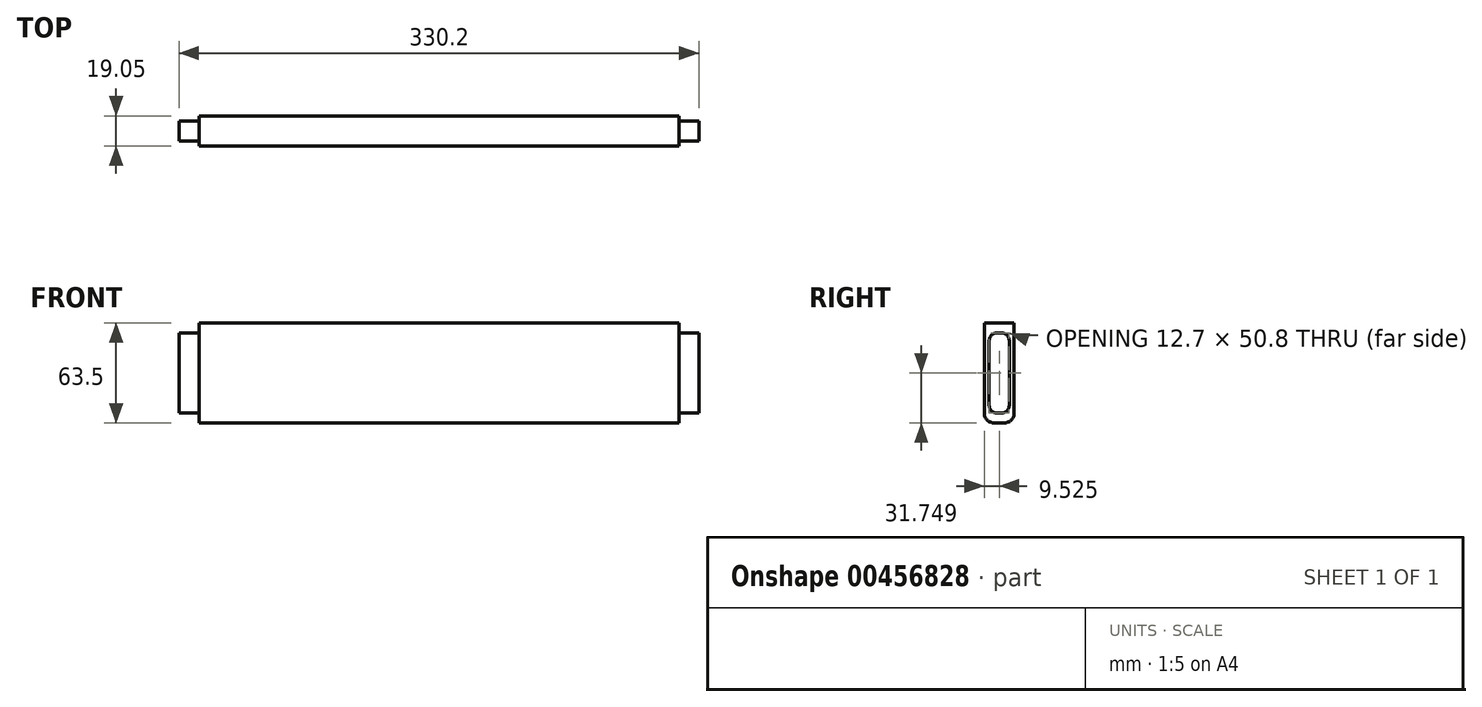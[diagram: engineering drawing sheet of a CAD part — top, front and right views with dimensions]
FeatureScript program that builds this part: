
annotation { "Feature Type Name" : "Feature", "Feature Type Description" : "" }
export const myFeature = defineFeature(function(context is Context, id is Id, definition is map)
    precondition{}
    {
        {
            var Q0;
            Q0=qCreatedBy(makeId("Front.planeOp"),FACE);
            var sketch = newSketch(context, id + "F0", { "sketchPlane" : qUnion([Q0])});
            skLineSegment(sketch, "E0.bottom", {"start": v(-64.17, 31.3) * mm, "end": v(240.63, 31.3) * mm});
            skLineSegment(sketch, "E0.top", {"start": v(-64.17, -32.2) * mm, "end": v(240.63, -32.2) * mm});
            skLineSegment(sketch, "E0.left", {"start": v(-64.17, 31.3) * mm, "end": v(-64.17, -32.2) * mm});
            skLineSegment(sketch, "E0.right", {"start": v(240.63, 31.3) * mm, "end": v(240.63, -32.2) * mm});
            skSolve(sketch);
        }
        {
            var Q0;
            Q0=makeQuery(id+"F0.imprint","IMPRINT",FACE,{"disambiguationData":[TD([[makeQuery(id+"F0.imprint","IMPRINT",EDGE,{"derivedFrom":sQuery(id+"F0.wireOp",EDGE,"E0.bottom")}),-1.0]])]});
            extrude(context, id + "F1", {"entities" : qUnion([Q0]), "oppositeDirection" : true, "depth" : 19.05 * mm});
        }
        {
            var Q0;
            Q0=makeQuery(id+"F1.opExtrude","SWEPT_FACE",FACE,{"disambiguationData":[OSD([sQuery(id+"F0.wireOp",EDGE,"E0.right")])]});
            var sketch = newSketch(context, id + "F2", { "sketchPlane" : qUnion([Q0])});
            skLineSegment(sketch, "E1.bottom", {"start": v(7.92, 24.95) * mm, "end": v(11.13, 24.95) * mm});
            skLineSegment(sketch, "E1.top", {"start": v(7.92, -25.85) * mm, "end": v(11.13, -25.85) * mm});
            skLineSegment(sketch, "E1.left", {"start": v(3.18, 20.2) * mm, "end": v(3.18, -21.1) * mm});
            skLineSegment(sketch, "E1.right", {"start": v(15.88, 20.2) * mm, "end": v(15.88, -21.1) * mm});
            skPoint(sketch, "E2.visualSharp", {"position": v(3.18, 24.95) * mm});
            skArc(sketch, "E2.filletArc", {"start": v(7.92, 24.95) * mm, "mid": v(4.57, 23.56) * mm, "end": v(3.18, 20.2) * mm});
            skPoint(sketch, "E3.visualSharp", {"position": v(15.88, 24.95) * mm});
            skArc(sketch, "E3.filletArc", {"start": v(15.88, 20.2) * mm, "mid": v(14.48, 23.56) * mm, "end": v(11.13, 24.95) * mm});
            skPoint(sketch, "E4.visualSharp", {"position": v(3.18, -25.85) * mm});
            skArc(sketch, "E4.filletArc", {"start": v(3.18, -21.1) * mm, "mid": v(4.57, -24.46) * mm, "end": v(7.92, -25.85) * mm});
            skPoint(sketch, "E5.visualSharp", {"position": v(15.88, -25.85) * mm});
            skArc(sketch, "E5.filletArc", {"start": v(11.13, -25.85) * mm, "mid": v(14.48, -24.46) * mm, "end": v(15.88, -21.1) * mm});
            skSolve(sketch);
        }
        {
            var Q0;
            Q0=makeQuery(id+"F2.imprint","IMPRINT",FACE,{"disambiguationData":[TD([[makeQuery(id+"F2.imprint","IMPRINT",EDGE,{"derivedFrom":sQuery(id+"F2.wireOp",EDGE,"E1.bottom")}),-1.0]])]});
            extrude(context, id + "F3", {"entities" : qUnion([Q0]), "operationType" : NewBodyOperationType.ADD, "depth" : 12.7 * mm});
        }
        {
            var Q0;
            Q0=makeQuery(id+"F1.opExtrude","SWEPT_FACE",FACE,{"disambiguationData":[OSD([sQuery(id+"F0.wireOp",EDGE,"E0.left")])]});
            var sketch = newSketch(context, id + "F4", { "sketchPlane" : qUnion([Q0])});
            skLineSegment(sketch, "E6.bottom", {"start": v(-11.13, 24.95) * mm, "end": v(-7.92, 24.95) * mm});
            skLineSegment(sketch, "E6.top", {"start": v(-11.13, -25.85) * mm, "end": v(-7.92, -25.85) * mm});
            skLineSegment(sketch, "E6.left", {"start": v(-15.88, 20.2) * mm, "end": v(-15.88, -21.1) * mm});
            skLineSegment(sketch, "E6.right", {"start": v(-3.17, 20.2) * mm, "end": v(-3.17, -21.1) * mm});
            skPoint(sketch, "E7.visualSharp", {"position": v(-15.88, 24.95) * mm});
            skArc(sketch, "E7.filletArc", {"start": v(-11.13, 24.95) * mm, "mid": v(-14.48, 23.56) * mm, "end": v(-15.88, 20.2) * mm});
            skPoint(sketch, "E8.visualSharp", {"position": v(-3.17, 24.95) * mm});
            skArc(sketch, "E8.filletArc", {"start": v(-3.17, 20.2) * mm, "mid": v(-4.57, 23.56) * mm, "end": v(-7.92, 24.95) * mm});
            skPoint(sketch, "E9.visualSharp", {"position": v(-3.17, -25.85) * mm});
            skArc(sketch, "E9.filletArc", {"start": v(-7.92, -25.85) * mm, "mid": v(-4.57, -24.46) * mm, "end": v(-3.17, -21.1) * mm});
            skPoint(sketch, "E10.visualSharp", {"position": v(-15.88, -25.85) * mm});
            skArc(sketch, "E10.filletArc", {"start": v(-15.88, -21.1) * mm, "mid": v(-14.48, -24.46) * mm, "end": v(-11.13, -25.85) * mm});
            skSolve(sketch);
        }
        {
            var Q0;
            Q0=makeQuery(id+"F4.imprint","IMPRINT",FACE,{"disambiguationData":[TD([[makeQuery(id+"F4.imprint","IMPRINT",EDGE,{"derivedFrom":sQuery(id+"F4.wireOp",EDGE,"E6.bottom")}),-1.0]])]});
            extrude(context, id + "F5", {"entities" : qUnion([Q0]), "operationType" : NewBodyOperationType.ADD, "depth" : 12.7 * mm});
        }
        {
            var Q0;
            Q0=makeQuery(id+"F1.opExtrude","CAP_EDGE",EDGE,{"disambiguationData":[OSD([sQuery(id+"F0.wireOp",EDGE,"E0.top")])],"isStart":true});
            var Q1;
            Q1=makeQuery(id+"F1.opExtrude","CAP_EDGE",EDGE,{"disambiguationData":[OSD([sQuery(id+"F0.wireOp",EDGE,"E0.top")])],"isStart":false});
            fillet(context, id + "F6", {"entities" : qUnion([Q0, Q1]), "radius" : 6.35 * mm, "tangentPropagation" : true, "allowEdgeOverflow" : false});
        }
    });
